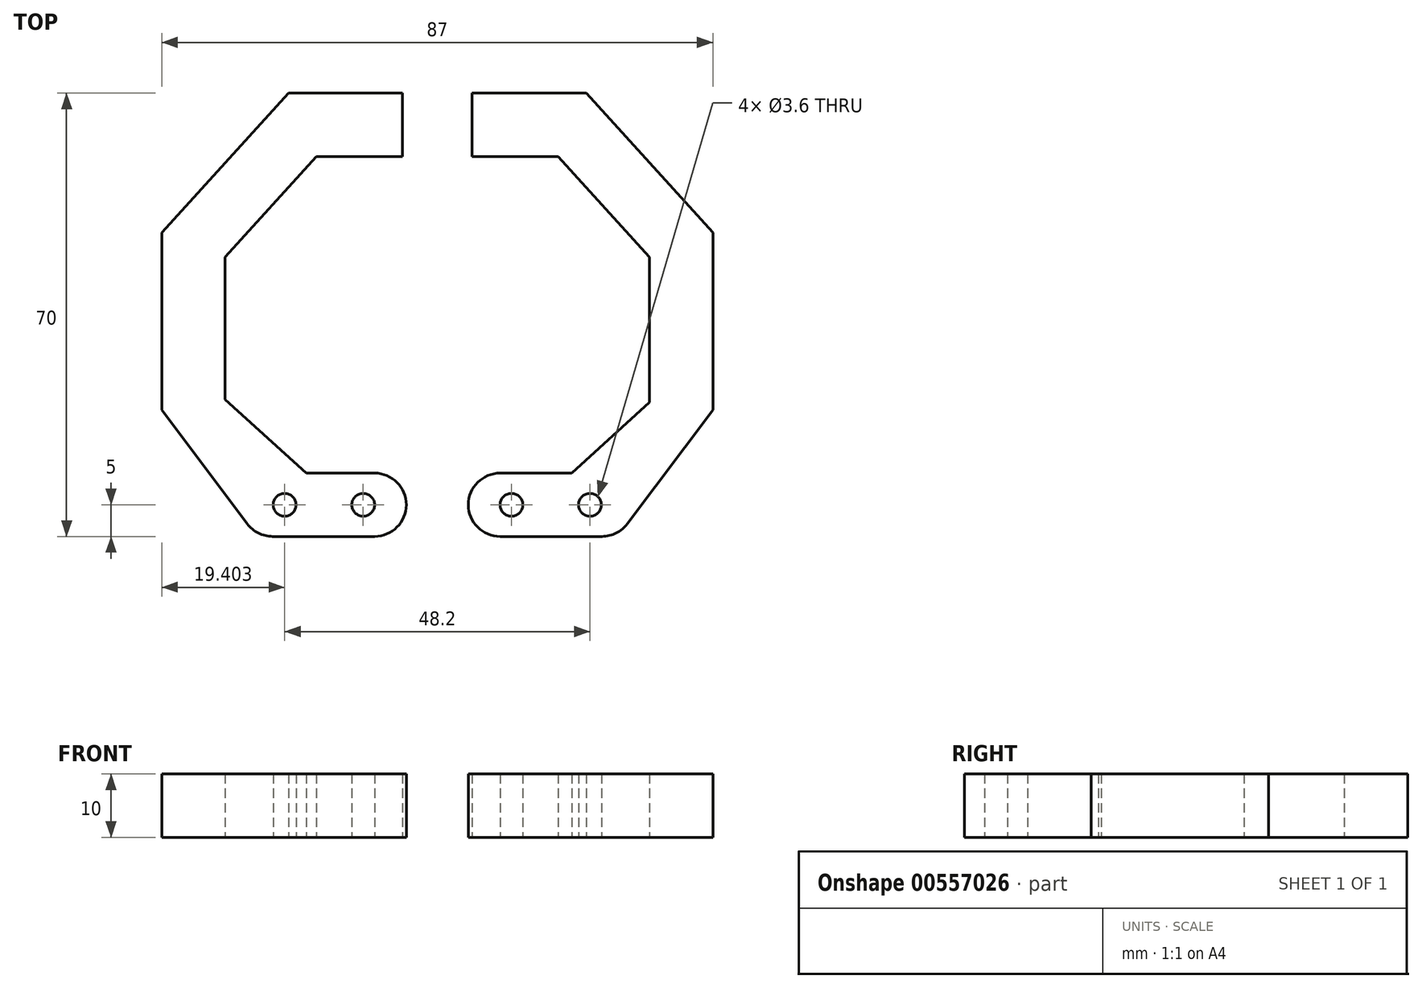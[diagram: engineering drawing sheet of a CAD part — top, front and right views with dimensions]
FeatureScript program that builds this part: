
annotation { "Feature Type Name" : "Feature", "Feature Type Description" : "" }
export const myFeature = defineFeature(function(context is Context, id is Id, definition is map)
    precondition{}
    {
        {
            var Q0;
            Q0=qCreatedBy(makeId("Top.planeOp"),FACE);
            var sketch = newSketch(context, id + "F0", { "sketchPlane" : qUnion([Q0])});
            skLineSegment(sketch, "E0.bottom", {"start": v(28.48, -32.9) * mm, "end": v(4.88, -32.9) * mm});
            skLineSegment(sketch, "E0.top", {"start": v(23.48, 37.1) * mm, "end": v(5.48, 37.1) * mm});
            skLineSegment(sketch, "E0.left", {"start": v(43.48, -12.9) * mm, "end": v(43.48, 15.1) * mm});
            skLineSegment(sketch, "E0.right", {"start": v(-43.52, -12.9) * mm, "end": v(-43.52, 15.1) * mm});
            skPoint(sketch, "E0.middle", {"position": v(-0.02, 2.1) * mm});
            skLineSegment(sketch, "E1", {"start": v(-43.52, -12.9) * mm, "end": v(-28.52, -32.9) * mm});
            skLineSegment(sketch, "E2", {"start": v(28.48, -32.9) * mm, "end": v(43.48, -12.9) * mm});
            skLineSegment(sketch, "E3", {"start": v(-43.52, 15.1) * mm, "end": v(-23.52, 37.1) * mm});
            skLineSegment(sketch, "E4", {"start": v(43.48, 15.1) * mm, "end": v(23.48, 37.1) * mm});
            skLineSegment(sketch, "E5", {"start": v(-23.52, 37.1) * mm, "end": v(-5.52, 37.1) * mm});
            skLineSegment(sketch, "E6", {"start": v(-5.52, 37.1) * mm, "end": v(-5.52, 27.1) * mm});
            skLineSegment(sketch, "E7", {"start": v(-5.52, 27.1) * mm, "end": v(-19.1, 27.1) * mm});
            skLineSegment(sketch, "E8", {"start": v(-19.1, 27.1) * mm, "end": v(-33.52, 11.23) * mm});
            skLineSegment(sketch, "E9", {"start": v(-33.52, 11.23) * mm, "end": v(-33.52, -11.26) * mm});
            skLineSegment(sketch, "E10", {"start": v(-33.52, -11.26) * mm, "end": v(-20.71, -22.9) * mm});
            skLineSegment(sketch, "E11", {"start": v(-20.71, -22.9) * mm, "end": v(-4.92, -22.9) * mm});
            skLineSegment(sketch, "E12", {"start": v(-4.92, -22.9) * mm, "end": v(-4.92, -32.9) * mm});
            skLineSegment(sketch, "E13", {"start": v(5.48, 37.1) * mm, "end": v(5.48, 27.1) * mm});
            skLineSegment(sketch, "E14", {"start": v(5.48, 27.1) * mm, "end": v(19.06, 27.1) * mm});
            skLineSegment(sketch, "E15", {"start": v(19.06, 27.1) * mm, "end": v(33.48, 11.23) * mm});
            skLineSegment(sketch, "E16", {"start": v(33.48, 11.23) * mm, "end": v(33.48, -11.72) * mm});
            skLineSegment(sketch, "E17", {"start": v(33.48, -11.72) * mm, "end": v(21.18, -22.9) * mm});
            skLineSegment(sketch, "E18", {"start": v(21.18, -22.9) * mm, "end": v(4.88, -22.9) * mm});
            skLineSegment(sketch, "E19", {"start": v(4.88, -22.9) * mm, "end": v(4.88, -32.9) * mm});
            skCircle(sketch, "E20", {"center": v(11.68, -27.9) * mm, "radius": 1.8 * mm});
            skCircle(sketch, "E21", {"center": v(-11.72, -27.9) * mm, "radius": 1.8 * mm});
            skCircle(sketch, "E22", {"center": v(24.08, -27.9) * mm, "radius": 1.8 * mm});
            skCircle(sketch, "E23", {"center": v(-24.12, -27.9) * mm, "radius": 1.8 * mm});
            skPoint(sketch, "E24.orphan", {"position": v(-43.52, 37.1) * mm});
            skLineSegment(sketch, "E25.trimOffspring", {"start": v(-5.52, 37.1) * mm, "end": v(-23.52, 37.1) * mm});
            skPoint(sketch, "E26.orphan", {"position": v(43.48, 37.1) * mm});
            skPoint(sketch, "E27.orphan", {"position": v(43.48, -32.9) * mm});
            skLineSegment(sketch, "E28.trimOffspring", {"start": v(-4.92, -32.9) * mm, "end": v(-28.52, -32.9) * mm});
            skPoint(sketch, "E29.orphan", {"position": v(-43.52, -32.9) * mm});
            skSolve(sketch);
        }
        {
            var Q0;
            Q0 = qSketchRegion(id + "F0", true);
            extrude(context, id + "F1", {"entities" : qUnion([Q0]), "depth" : 10 * mm, "offsetDistance" : 25 * mm});
        }
        {
            var Q0;
            Q0=makeQuery(id+"F1.opExtrude","SWEPT_EDGE",EDGE,{"disambiguationData":[OSD([sQuery(id+"F0.wireOp",EDGE,"E12"),sQuery(id+"F0.wireOp",EDGE,"E28.trimOffspring")])]});
            var Q1;
            Q1=makeQuery(id+"F1.opExtrude","SWEPT_EDGE",EDGE,{"disambiguationData":[OSD([sQuery(id+"F0.wireOp",EDGE,"E11"),sQuery(id+"F0.wireOp",EDGE,"E12")])]});
            var Q2;
            Q2=makeQuery(id+"F1.opExtrude","SWEPT_EDGE",EDGE,{"disambiguationData":[OSD([sQuery(id+"F0.wireOp",EDGE,"E18"),sQuery(id+"F0.wireOp",EDGE,"E19")])]});
            var Q3;
            Q3=makeQuery(id+"F1.opExtrude","SWEPT_EDGE",EDGE,{"disambiguationData":[OSD([sQuery(id+"F0.wireOp",EDGE,"E0.bottom"),sQuery(id+"F0.wireOp",EDGE,"E19")])]});
            fillet(context, id + "F2", {"entities" : qUnion([Q0, Q1, Q2, Q3]), "radius" : 5 * mm, "tangentPropagation" : true, "allowEdgeOverflow" : false});
        }
        {
            var Q0;
            Q0=makeQuery(id+"F1.opExtrude","SWEPT_EDGE",EDGE,{"disambiguationData":[OSD([sQuery(id+"F0.wireOp",EDGE,"E1"),sQuery(id+"F0.wireOp",EDGE,"E28.trimOffspring")])]});
            var Q1;
            Q1=makeQuery(id+"F1.opExtrude","SWEPT_EDGE",EDGE,{"disambiguationData":[OSD([sQuery(id+"F0.wireOp",EDGE,"E0.bottom"),sQuery(id+"F0.wireOp",EDGE,"E2")])]});
            fillet(context, id + "F3", {"entities" : qUnion([Q0, Q1]), "radius" : 5 * mm, "tangentPropagation" : true, "allowEdgeOverflow" : false});
        }
    });
